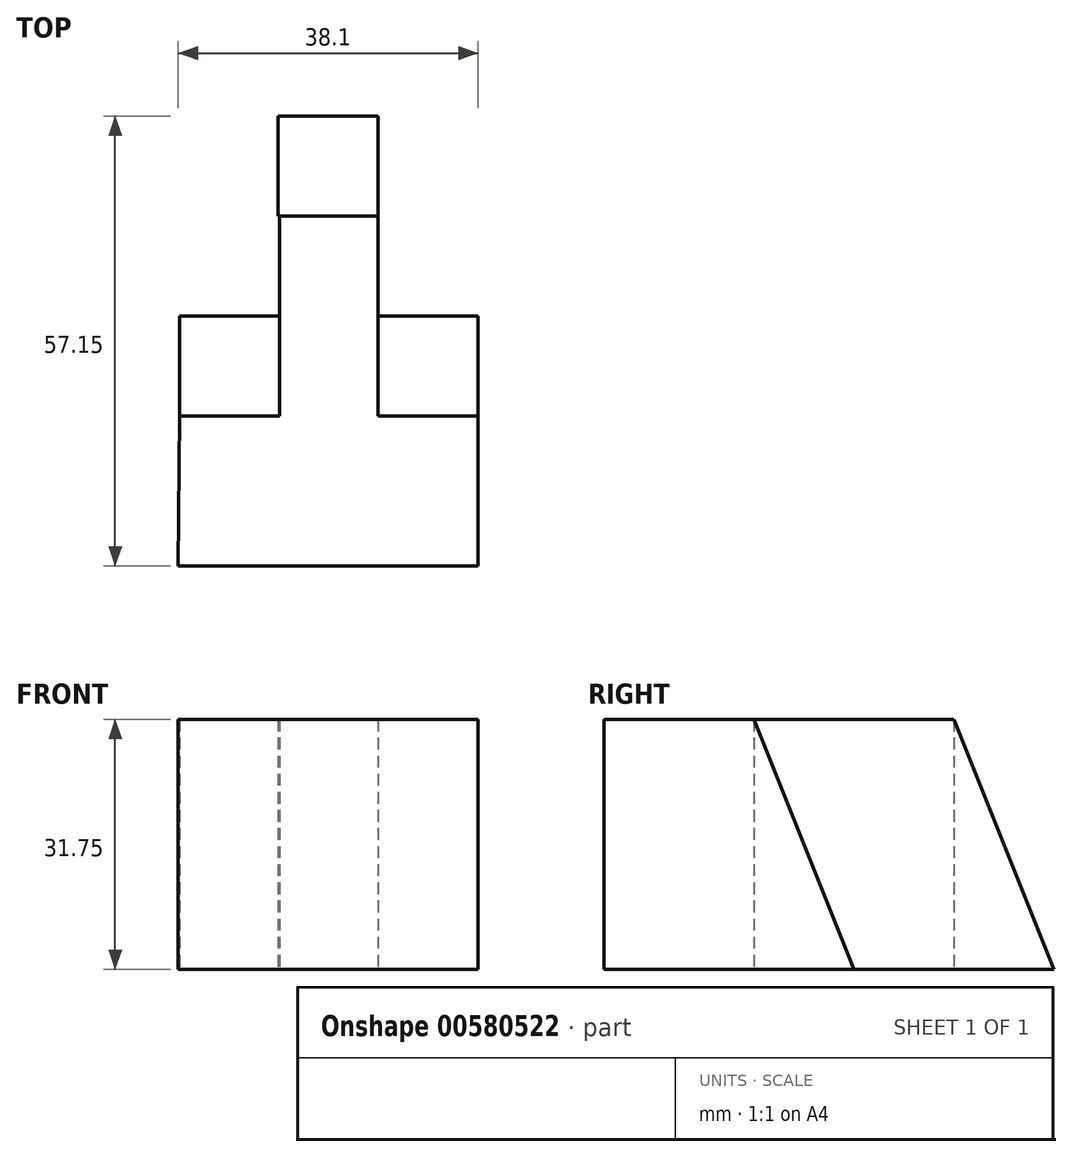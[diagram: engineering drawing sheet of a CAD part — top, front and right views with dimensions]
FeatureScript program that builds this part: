
annotation { "Feature Type Name" : "Feature", "Feature Type Description" : "" }
export const myFeature = defineFeature(function(context is Context, id is Id, definition is map)
    precondition{}
    {
        {
            var Q0;
            Q0=qCreatedBy(makeId("Top.planeOp"),FACE);
            var sketch = newSketch(context, id + "F0", { "sketchPlane" : qUnion([Q0])});
            skLineSegment(sketch, "E0", {"start": v(-53.38, -56.35) * mm, "end": v(-15.28, -56.35) * mm});
            skLineSegment(sketch, "E1", {"start": v(-15.28, -56.35) * mm, "end": v(-15.28, -37.3) * mm});
            skLineSegment(sketch, "E2", {"start": v(-15.28, -37.3) * mm, "end": v(-27.98, -37.3) * mm});
            skLineSegment(sketch, "E3", {"start": v(-27.98, -37.3) * mm, "end": v(-27.98, -11.9) * mm});
            skLineSegment(sketch, "E4", {"start": v(-27.98, -11.9) * mm, "end": v(-40.48, -11.9) * mm});
            skLineSegment(sketch, "E5", {"start": v(-40.48, -11.9) * mm, "end": v(-40.48, -37.3) * mm});
            skLineSegment(sketch, "E6", {"start": v(-40.48, -37.3) * mm, "end": v(-53.18, -37.3) * mm});
            skLineSegment(sketch, "E7", {"start": v(-53.18, -37.3) * mm, "end": v(-53.38, -56.35) * mm});
            skSolve(sketch);
        }
        {
            var Q0;
            Q0 = qSketchRegion(id + "F0", true);
            extrude(context, id + "F1", {"entities" : qUnion([Q0]), "depth" : 31.75 * mm, "offsetDistance" : 25.4 * mm});
        }
        {
            var Q0;
            Q0=makeQuery(id+"F1.opExtrude","SWEPT_FACE",FACE,{"disambiguationData":[OSD([sQuery(id+"F0.wireOp",EDGE,"E3")])]});
            var sketch = newSketch(context, id + "F2", { "sketchPlane" : qUnion([Q0])});
            skLineSegment(sketch, "E8", {"start": v(-37.3, 31.75) * mm, "end": v(-24.6, 0) * mm});
            skLineSegment(sketch, "E9", {"start": v(-24.6, 0) * mm, "end": v(-37.3, 0) * mm});
            skLineSegment(sketch, "E10", {"start": v(-37.3, 0) * mm, "end": v(-37.3, 31.75) * mm});
            skSolve(sketch);
        }
        {
            var Q0;
            Q0 = qSketchRegion(id + "F2", true);
            extrude(context, id + "F3", {"entities" : qUnion([Q0]), "operationType" : NewBodyOperationType.ADD, "depth" : 12.7 * mm, "offsetDistance" : 25.4 * mm});
        }
        {
            var Q0;
            Q0=makeQuery(id+"F1.opExtrude","SWEPT_FACE",FACE,{"disambiguationData":[OSD([sQuery(id+"F0.wireOp",EDGE,"E5")])]});
            var sketch = newSketch(context, id + "F4", { "sketchPlane" : qUnion([Q0])});
            skLineSegment(sketch, "E11", {"start": v(37.3, 31.75) * mm, "end": v(24.6, 0) * mm});
            skLineSegment(sketch, "E12", {"start": v(24.6, 0) * mm, "end": v(37.3, 0) * mm});
            skLineSegment(sketch, "E13", {"start": v(37.3, 0) * mm, "end": v(37.3, 31.75) * mm});
            skSolve(sketch);
        }
        {
            var Q0;
            Q0 = qSketchRegion(id + "F4", true);
            extrude(context, id + "F5", {"entities" : qUnion([Q0]), "operationType" : NewBodyOperationType.ADD, "depth" : 12.7 * mm, "offsetDistance" : 25.4 * mm});
        }
        {
            var Q0;
            Q0=makeQuery(id+"F1.opExtrude","SWEPT_FACE",FACE,{"disambiguationData":[OSD([sQuery(id+"F0.wireOp",EDGE,"E3")])]});
            var sketch = newSketch(context, id + "F6", { "sketchPlane" : qUnion([Q0])});
            skLineSegment(sketch, "E14", {"start": v(-11.9, 31.75) * mm, "end": v(0.8, 0) * mm});
            skLineSegment(sketch, "E15", {"start": v(0.8, 0) * mm, "end": v(-11.9, 0) * mm});
            skLineSegment(sketch, "E16", {"start": v(-11.9, 0) * mm, "end": v(-11.9, 31.75) * mm});
            skSolve(sketch);
        }
        {
            var Q0;
            Q0 = qSketchRegion(id + "F6", true);
            extrude(context, id + "F7", {"entities" : qUnion([Q0]), "operationType" : NewBodyOperationType.ADD, "oppositeDirection" : true, "depth" : 12.7 * mm, "offsetDistance" : 25.4 * mm});
        }
    });
